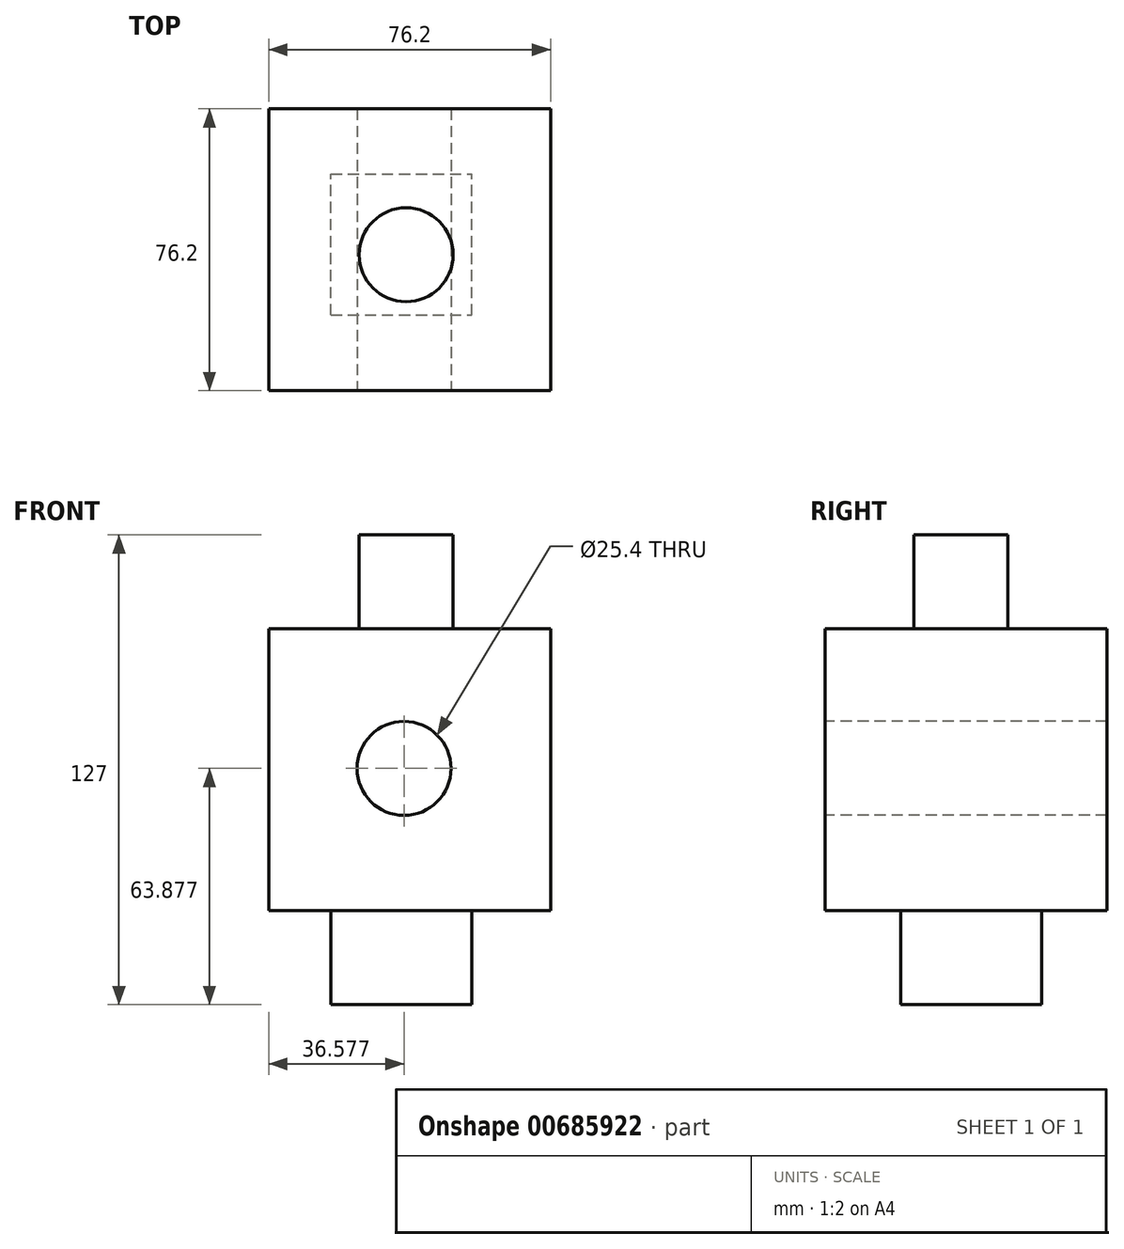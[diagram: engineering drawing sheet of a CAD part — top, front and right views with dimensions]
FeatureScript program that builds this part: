
annotation { "Feature Type Name" : "Feature", "Feature Type Description" : "" }
export const myFeature = defineFeature(function(context is Context, id is Id, definition is map)
    precondition{}
    {
        {
            var Q0;
            Q0=qCreatedBy(makeId("Top.planeOp"),FACE);
            var sketch = newSketch(context, id + "F0", { "sketchPlane" : qUnion([Q0])});
            skLineSegment(sketch, "E0", {"start": v(0, 0) * mm, "end": v(0, 76.2) * mm});
            skLineSegment(sketch, "E1", {"start": v(0, 76.2) * mm, "end": v(-76.2, 76.2) * mm});
            skLineSegment(sketch, "E2", {"start": v(-76.2, 76.2) * mm, "end": v(-76.2, 0) * mm});
            skLineSegment(sketch, "E3", {"start": v(-76.2, 0) * mm, "end": v(0, 0) * mm});
            skSolve(sketch);
        }
        {
            var Q0;
            Q0 = qSketchRegion(id + "F0", true);
            extrude(context, id + "F1", {"entities" : qUnion([Q0]), "depth" : 76.2 * mm, "offsetDistance" : 25.4 * mm});
        }
        {
            var Q0;
            Q0=makeQuery(id+"F1.opExtrude","SWEPT_FACE",FACE,{"disambiguationData":[OSD([sQuery(id+"F0.wireOp",EDGE,"E3")])]});
            var sketch = newSketch(context, id + "F2", { "sketchPlane" : qUnion([Q0])});
            skCircle(sketch, "E4", {"center": v(-39.62, 38.48) * mm, "radius": 12.7 * mm});
            skSolve(sketch);
        }
        {
            var Q0;
            Q0 = qSketchRegion(id + "F2", true);
            extrude(context, id + "F3", {"entities" : qUnion([Q0]), "operationType" : NewBodyOperationType.REMOVE, "oppositeDirection" : true, "depth" : 76.2 * mm, "offsetDistance" : 25.4 * mm});
        }
        {
            var Q0;
            Q0=makeQuery(id+"F1.opExtrude","CAP_FACE",FACE,{"disambiguationData":[OSD([sQuery(id+"F0.wireOp",EDGE,"E0"),sQuery(id+"F0.wireOp",EDGE,"E1"),sQuery(id+"F0.wireOp",EDGE,"E2"),sQuery(id+"F0.wireOp",EDGE,"E3")])],"isStart":false});
            var sketch = newSketch(context, id + "F4", { "sketchPlane" : qUnion([Q0])});
            skCircle(sketch, "E5", {"center": v(-39.05, 36.76) * mm, "radius": 12.7 * mm});
            skSolve(sketch);
        }
        {
            var Q0;
            Q0=makeQuery(id+"F4.imprint","IMPRINT",FACE,{"disambiguationData":[TD([[makeQuery(id+"F4.imprint","IMPRINT",EDGE,{"derivedFrom":sQuery(id+"F4.wireOp",EDGE,"E5")}),1.0]])]});
            extrude(context, id + "F5", {"entities" : qUnion([Q0]), "operationType" : NewBodyOperationType.ADD, "depth" : 25.4 * mm, "offsetDistance" : 25.4 * mm});
        }
        {
            var Q0;
            Q0=makeQuery(id+"F1.opExtrude","CAP_FACE",FACE,{"disambiguationData":[OSD([sQuery(id+"F0.wireOp",EDGE,"E0"),sQuery(id+"F0.wireOp",EDGE,"E1"),sQuery(id+"F0.wireOp",EDGE,"E2"),sQuery(id+"F0.wireOp",EDGE,"E3")])],"isStart":true});
            var sketch = newSketch(context, id + "F6", { "sketchPlane" : qUnion([Q0])});
            skLineSegment(sketch, "E6.bottom", {"start": v(-59.4, -20.43) * mm, "end": v(-21.3, -20.43) * mm});
            skLineSegment(sketch, "E6.top", {"start": v(-59.4, -58.53) * mm, "end": v(-21.3, -58.53) * mm});
            skLineSegment(sketch, "E6.left", {"start": v(-59.4, -20.43) * mm, "end": v(-59.4, -58.53) * mm});
            skLineSegment(sketch, "E6.right", {"start": v(-21.3, -20.43) * mm, "end": v(-21.3, -58.53) * mm});
            skSolve(sketch);
        }
        {
            var Q0;
            Q0=makeQuery(id+"F6.imprint","IMPRINT",FACE,{"disambiguationData":[TD([[makeQuery(id+"F6.imprint","IMPRINT",EDGE,{"derivedFrom":sQuery(id+"F6.wireOp",EDGE,"E6.bottom")}),-1.0]])]});
            extrude(context, id + "F7", {"entities" : qUnion([Q0]), "operationType" : NewBodyOperationType.ADD, "depth" : 25.4 * mm, "offsetDistance" : 25.4 * mm});
        }
    });
